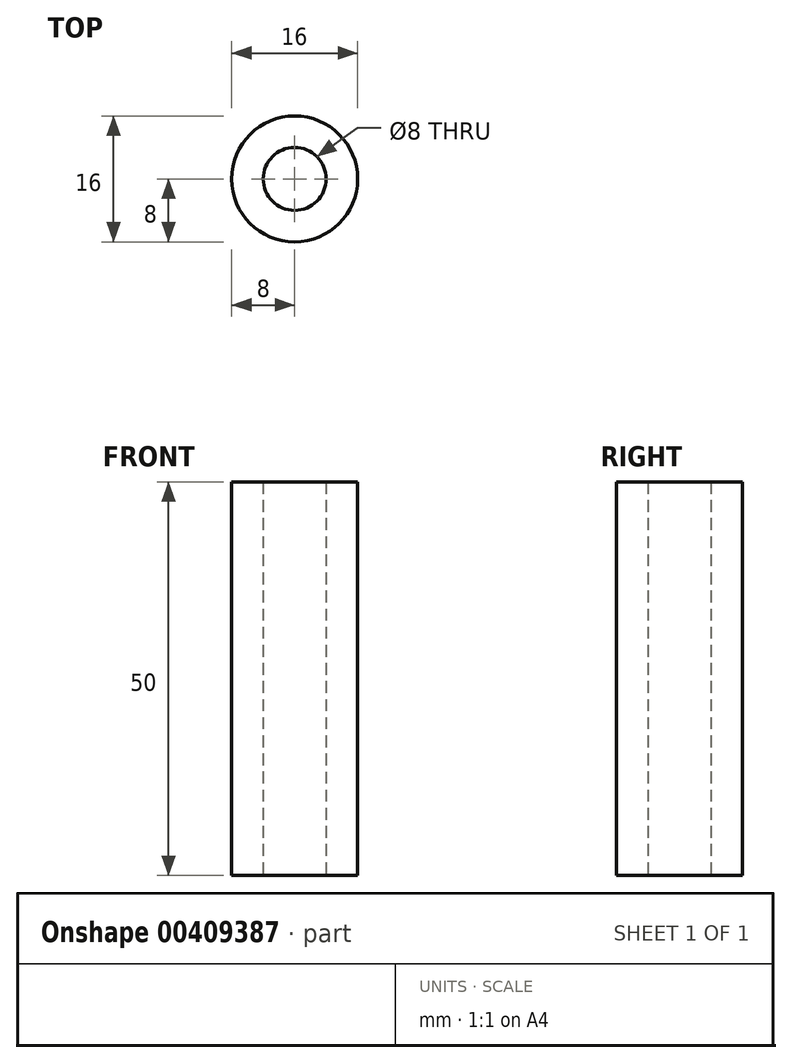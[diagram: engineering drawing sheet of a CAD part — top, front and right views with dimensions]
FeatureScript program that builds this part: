
annotation { "Feature Type Name" : "Feature", "Feature Type Description" : "" }
export const myFeature = defineFeature(function(context is Context, id is Id, definition is map)
    precondition{}
    {
        {
            var Q0;
            Q0=qCreatedBy(makeId("Top.planeOp"),FACE);
            var sketch = newSketch(context, id + "F0", { "sketchPlane" : qUnion([Q0])});
            skCircle(sketch, "E0", {"center": v(0, 0) * mm, "radius": 8 * mm});
            skCircle(sketch, "E1", {"center": v(0, 0) * mm, "radius": 4 * mm});
            skSolve(sketch);
        }
        {
            var Q0;
            Q0=makeQuery(id+"F0.imprint","IMPRINT",FACE,{"disambiguationData":[TD([[makeQuery(id+"F0.imprint","IMPRINT",EDGE,{"derivedFrom":sQuery(id+"F0.wireOp",EDGE,"E0")}),1.0]])]});
            extrude(context, id + "F1", {"entities" : qUnion([Q0]), "depth" : 50 * mm});
        }
    });
